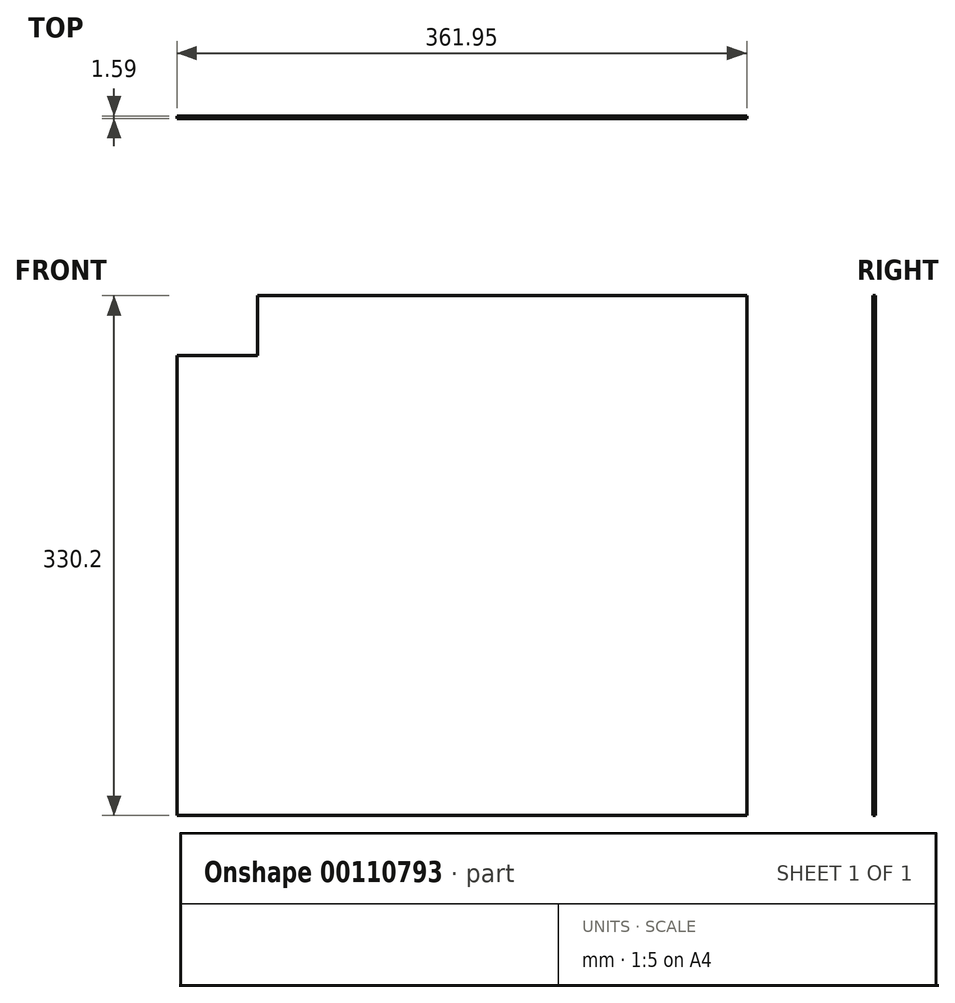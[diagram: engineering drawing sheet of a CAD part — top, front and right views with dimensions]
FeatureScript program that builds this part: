
annotation { "Feature Type Name" : "Feature", "Feature Type Description" : "" }
export const myFeature = defineFeature(function(context is Context, id is Id, definition is map)
    precondition{}
    {
        {
            var Q0;
            Q0=qCreatedBy(makeId("Front.planeOp"),FACE);
            var sketch = newSketch(context, id + "F0", { "sketchPlane" : qUnion([Q0])});
            skLineSegment(sketch, "E0.bottom", {"start": v(-161.04, 290.88) * mm, "end": v(200.9, 290.88) * mm});
            skLineSegment(sketch, "E0.top", {"start": v(-161.04, -39.32) * mm, "end": v(200.9, -39.32) * mm});
            skLineSegment(sketch, "E0.left", {"start": v(-161.04, 290.88) * mm, "end": v(-161.04, -39.32) * mm});
            skLineSegment(sketch, "E0.right", {"start": v(200.9, 290.88) * mm, "end": v(200.9, -39.32) * mm});
            skSolve(sketch);
        }
        {
            var Q0;
            Q0=makeQuery(id+"F0.imprint","IMPRINT",FACE,{"disambiguationData":[TD([[makeQuery(id+"F0.imprint","IMPRINT",EDGE,{"derivedFrom":sQuery(id+"F0.wireOp",EDGE,"E0.bottom")}),-1.0]])]});
            extrude(context, id + "F1", {"entities" : qUnion([Q0]), "depth" : 1.59 * mm});
        }
        {
            var Q0;
            Q0=makeQuery(id+"F1.opExtrude","CAP_FACE",FACE,{"disambiguationData":[OSD([sQuery(id+"F0.wireOp",EDGE,"E0.bottom"),sQuery(id+"F0.wireOp",EDGE,"E0.top"),sQuery(id+"F0.wireOp",EDGE,"E0.left"),sQuery(id+"F0.wireOp",EDGE,"E0.right")])],"isStart":false});
            var sketch = newSketch(context, id + "F2", { "sketchPlane" : qUnion([Q0])});
            skSolve(sketch);
        }
        {
            var Q0;
            Q0=makeQuery(id+"F2.imprint","IMPRINT",FACE,{"disambiguationData":[TD([[makeQuery(id+"F2.imprint","IMPRINT",EDGE,{"derivedFrom":makeQuery(id+"F1.opExtrude","CAP_EDGE",EDGE,{"disambiguationData":[OSD([sQuery(id+"F0.wireOp",EDGE,"E0.bottom")])],"isStart":false})}),-1.0]])]});
            var sketch = newSketch(context, id + "F3", { "sketchPlane" : qUnion([Q0])});
            skLineSegment(sketch, "E1.bottom", {"start": v(-161.98, 291.5) * mm, "end": v(-109.68, 291.5) * mm});
            skLineSegment(sketch, "E1.top", {"start": v(-161.98, 252.95) * mm, "end": v(-109.68, 252.95) * mm});
            skLineSegment(sketch, "E1.left", {"start": v(-161.98, 291.5) * mm, "end": v(-161.98, 252.95) * mm});
            skLineSegment(sketch, "E1.right", {"start": v(-109.68, 291.5) * mm, "end": v(-109.68, 252.95) * mm});
            skSolve(sketch);
        }
        {
            var Q0;
            Q0 = qSketchRegion(id + "F3", true);
            extrude(context, id + "F4", {"entities" : qUnion([Q0]), "operationType" : NewBodyOperationType.REMOVE, "oppositeDirection" : true, "depth" : 25.4 * mm});
        }
    });
